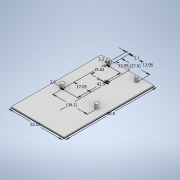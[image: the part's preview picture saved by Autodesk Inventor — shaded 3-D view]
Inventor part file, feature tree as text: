
AUTODESK INVENTOR PART (.ipt)
format: ipt  version: 2020 (Build 240168000, 168)  size: 135,168 bytes
history: native  units: mm
features: sketch x3, extrude x3
ambient origin geometry x8: Origin, YZ Plane, XZ Plane, XY Plane, X Axis, Y Axis, Z Axis, Center Point
bodies: Solid1 (feature_tree)
feature tree (6):
  sketch  "Sketch1"  dims[d0=52.05mm d1=88.8mm]
  sketch  "Sketch2"  dims[d2=3.8mm d4=17.05mm]
  extrude  "Extrusion1"  Depth=88.8mm
  sketch  "Sketch3"  dims[d5=3.2mm d6=13.95mm d7=42.5mm d8=5.0mm d9=0.0mm d10=1.0mm d11=0.0mm d12=4.83mm d13=4.0mm d15=5.0mm d16=0.0mm d17=15.62mm d18=27.9mm d19=3.1mm d20=13.95mm d21=34.1mm]
  extrude  "Extrusion2"  Depth=17.05mm
  extrude  "Extrusion3"  Depth=5.0mm
